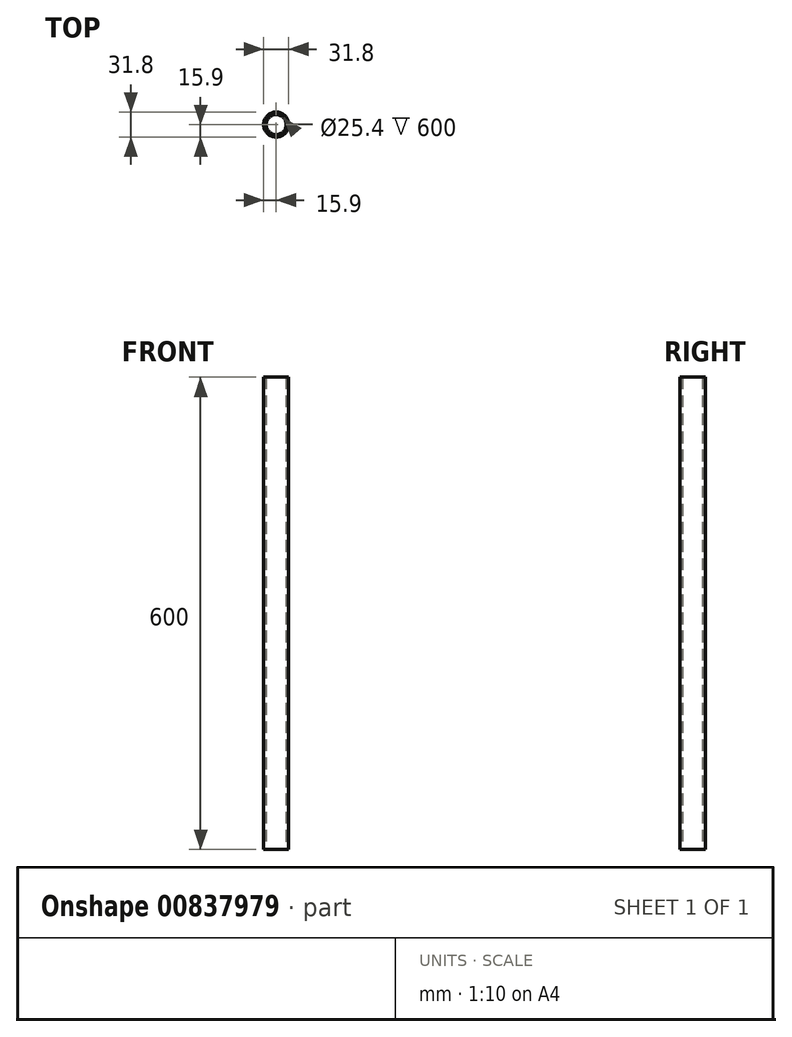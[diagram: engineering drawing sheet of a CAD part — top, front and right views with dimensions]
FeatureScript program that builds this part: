
annotation { "Feature Type Name" : "Feature", "Feature Type Description" : "" }
export const myFeature = defineFeature(function(context is Context, id is Id, definition is map)
    precondition{}
    {
        {
            var Q0;
            Q0=qCreatedBy(makeId("Top.planeOp"),FACE);
            var sketch = newSketch(context, id + "F0", { "sketchPlane" : qUnion([Q0])});
            skCircle(sketch, "E0", {"center": v(0, 0) * mm, "radius": 15.9 * mm});
            skCircle(sketch, "E1", {"center": v(0, 0) * mm, "radius": 12.7 * mm});
            skSolve(sketch);
        }
        {
            var Q0;
            Q0 = qSketchRegion(id + "F0", true);
            extrude(context, id + "F1", {"entities" : qUnion([Q0]), "depth" : 600 * mm, "offsetDistance" : 25 * mm});
        }
    });
